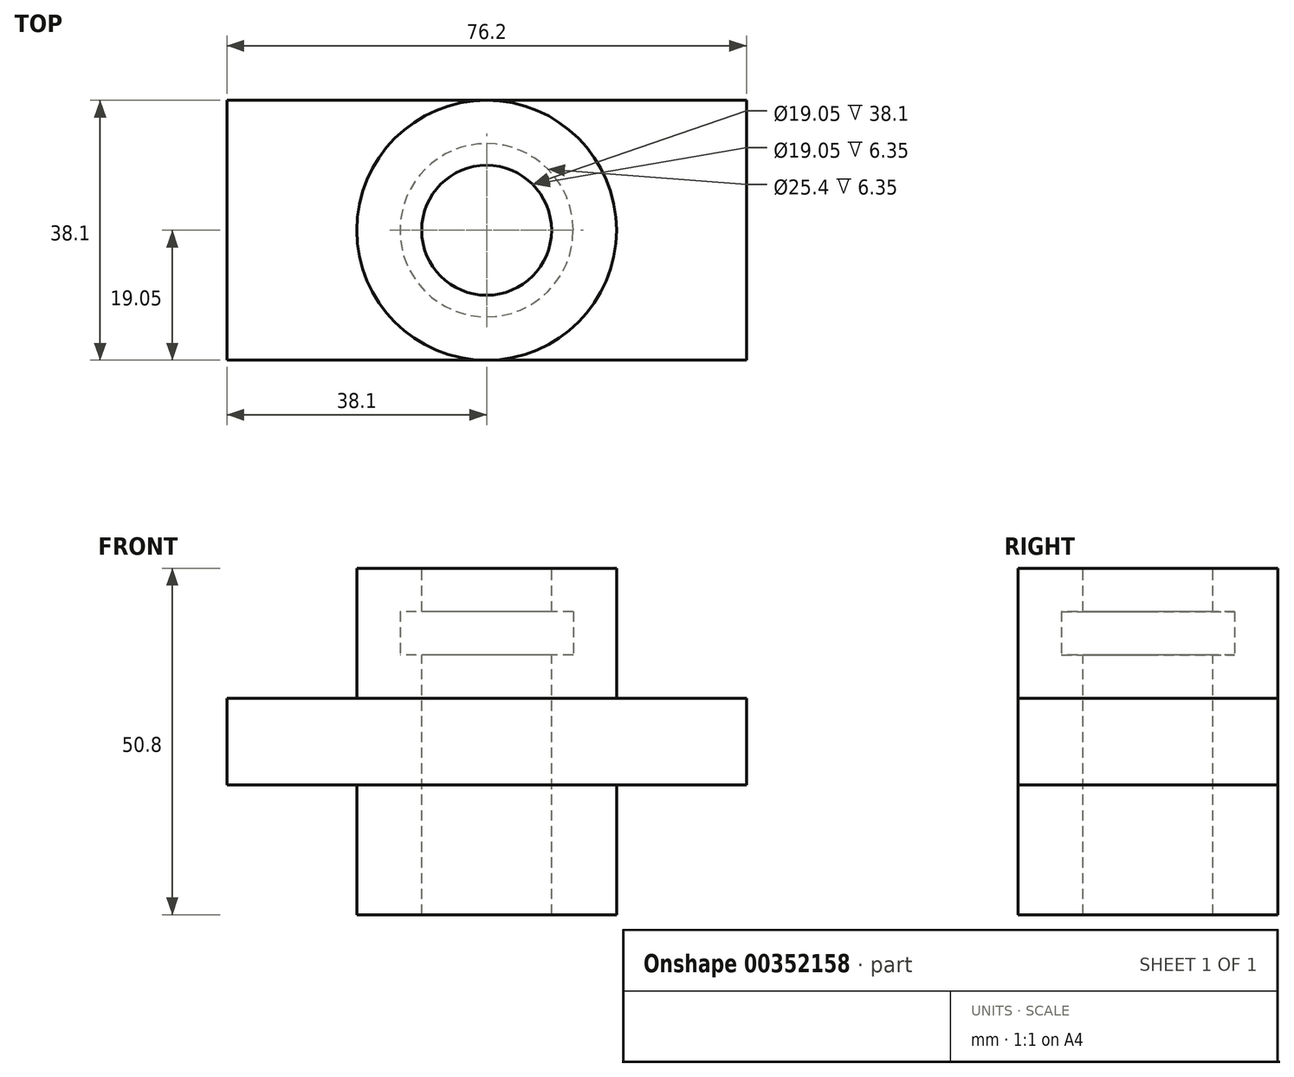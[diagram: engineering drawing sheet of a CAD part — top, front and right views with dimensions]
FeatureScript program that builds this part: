
annotation { "Feature Type Name" : "Feature", "Feature Type Description" : "" }
export const myFeature = defineFeature(function(context is Context, id is Id, definition is map)
    precondition{}
    {
        {
            var Q0;
            Q0=qCreatedBy(makeId("Top.planeOp"),FACE);
            var sketch = newSketch(context, id + "F0", { "sketchPlane" : qUnion([Q0])});
            skLineSegment(sketch, "E0.bottom", {"start": v(-38.1, 19.05) * mm, "end": v(38.1, 19.05) * mm});
            skLineSegment(sketch, "E0.top", {"start": v(-38.1, -19.05) * mm, "end": v(38.1, -19.05) * mm});
            skLineSegment(sketch, "E0.left", {"start": v(-38.1, 19.05) * mm, "end": v(-38.1, -19.05) * mm});
            skLineSegment(sketch, "E0.right", {"start": v(38.1, 19.05) * mm, "end": v(38.1, -19.05) * mm});
            skSolve(sketch);
        }
        {
            var Q0;
            Q0=makeQuery(id+"F0.imprint","IMPRINT",FACE,{"disambiguationData":[TD([[makeQuery(id+"F0.imprint","IMPRINT",EDGE,{"derivedFrom":sQuery(id+"F0.wireOp",EDGE,"E0.bottom")}),-1.0]])]});
            extrude(context, id + "F1", {"entities" : qUnion([Q0]), "endBound" : BoundingType.SYMMETRIC, "depth" : 12.7 * mm});
        }
        {
            var Q0;
            Q0=qCreatedBy(makeId("Top.planeOp"),FACE);
            var sketch = newSketch(context, id + "F2", { "sketchPlane" : qUnion([Q0])});
            skCircle(sketch, "E1", {"center": v(0, 0) * mm, "radius": 19.05 * mm});
            skSolve(sketch);
        }
        {
            var Q0;
            Q0 = qSketchRegion(id + "F2", true);
            extrude(context, id + "F3", {"entities" : qUnion([Q0]), "operationType" : NewBodyOperationType.ADD, "endBound" : BoundingType.SYMMETRIC, "depth" : 50.8 * mm});
        }
        {
            var Q0;
            Q0=qCreatedBy(makeId("Top.planeOp"),FACE);
            var sketch = newSketch(context, id + "F4", { "sketchPlane" : qUnion([Q0])});
            skCircle(sketch, "E2", {"center": v(0, 0) * mm, "radius": 9.53 * mm});
            skSolve(sketch);
        }
        {
            var Q0;
            Q0 = qSketchRegion(id + "F4", true);
            extrude(context, id + "F5", {"entities" : qUnion([Q0]), "operationType" : NewBodyOperationType.REMOVE, "endBound" : BoundingType.THROUGH_ALL, "oppositeDirection" : true, "depth" : 25.4 * mm, "hasSecondDirection" : true, "secondDirectionBound" : SecondDirectionBoundingType.THROUGH_ALL, "secondDirectionOppositeDirection" : false, "secondDirectionDepth" : 25.4 * mm});
        }
        {
            var Q0;
            Q0=qCreatedBy(makeId("Top.planeOp"),FACE);
            var sketch = newSketch(context, id + "F6", { "sketchPlane" : qUnion([Q0])});
            skCircle(sketch, "E3", {"center": v(0, 0) * mm, "radius": 12.7 * mm});
            skSolve(sketch);
        }
        {
            var Q0;
            Q0 = qSketchRegion(id + "F6", true);
            extrude(context, id + "F7", {"entities" : qUnion([Q0]), "operationType" : NewBodyOperationType.REMOVE, "depth" : 19.05 * mm, "hasSecondDirection" : true, "secondDirectionOppositeDirection" : false, "secondDirectionDepth" : 12.7 * mm});
        }
    });
